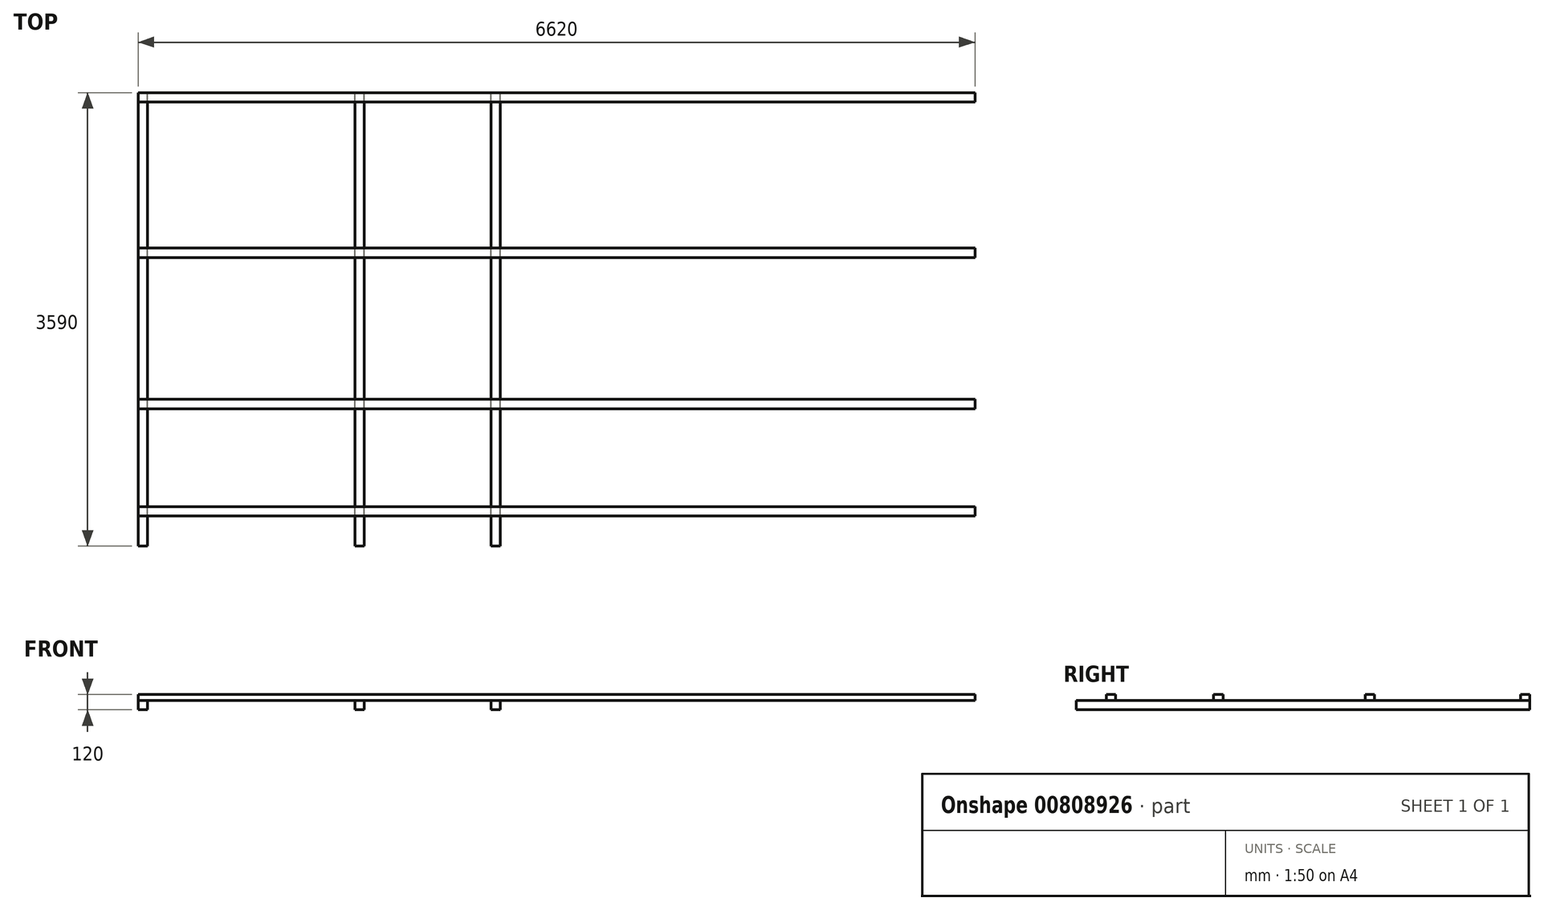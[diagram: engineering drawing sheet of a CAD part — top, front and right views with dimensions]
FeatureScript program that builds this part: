
annotation { "Feature Type Name" : "Feature", "Feature Type Description" : "" }
export const myFeature = defineFeature(function(context is Context, id is Id, definition is map)
    precondition{}
    {
        {
            var Q0;
            Q0=qCreatedBy(makeId("Front.planeOp"),FACE);
            var sketch = newSketch(context, id + "F0", { "sketchPlane" : qUnion([Q0])});
            skLineSegment(sketch, "E0.bottom", {"start": v(0, -75) * mm, "end": v(75, -75) * mm});
            skLineSegment(sketch, "E0.top", {"start": v(0, 0) * mm, "end": v(75, 0) * mm});
            skLineSegment(sketch, "E0.left", {"start": v(0, -75) * mm, "end": v(0, 0) * mm});
            skLineSegment(sketch, "E0.right", {"start": v(75, -75) * mm, "end": v(75, 0) * mm});
            skLineSegment(sketch, "E1.bottom", {"start": v(1714.03, -75) * mm, "end": v(1789.03, -75) * mm});
            skLineSegment(sketch, "E1.top", {"start": v(1714.03, 0) * mm, "end": v(1789.03, 0) * mm});
            skLineSegment(sketch, "E1.left", {"start": v(1714.03, -75) * mm, "end": v(1714.03, 0) * mm});
            skLineSegment(sketch, "E1.right", {"start": v(1789.03, -75) * mm, "end": v(1789.03, 0) * mm});
            skLineSegment(sketch, "E2.bottom", {"start": v(2790.5, -75) * mm, "end": v(2865.5, -75) * mm});
            skLineSegment(sketch, "E2.top", {"start": v(2790.5, 0) * mm, "end": v(2865.5, 0) * mm});
            skLineSegment(sketch, "E2.left", {"start": v(2790.5, -75) * mm, "end": v(2790.5, 0) * mm});
            skLineSegment(sketch, "E2.right", {"start": v(2865.5, -75) * mm, "end": v(2865.5, 0) * mm});
            skSolve(sketch);
        }
        {
            var Q0;
            Q0=qCreatedBy(makeId("Top.planeOp"),FACE);
            var sketch = newSketch(context, id + "F1", { "sketchPlane" : qUnion([Q0])});
            skLineSegment(sketch, "E3.top", {"start": v(0, 0) * mm, "end": v(6620, 0) * mm});
            skLineSegment(sketch, "E4.MirrorCS", {"start": v(6620, -75) * mm, "end": v(6620, 0) * mm});
            skLineSegment(sketch, "E5.MirrorCS", {"start": v(6620, -2502.27) * mm, "end": v(6620, -2427.27) * mm});
            skLineSegment(sketch, "E6.MirrorCS", {"start": v(0, -2502.27) * mm, "end": v(0, -2427.27) * mm});
            skLineSegment(sketch, "E7.MirrorCS", {"start": v(0, -1304.62) * mm, "end": v(0, -1229.62) * mm});
            skLineSegment(sketch, "E8.MirrorCS", {"start": v(6620, -1304.62) * mm, "end": v(6620, -1229.62) * mm});
            skLineSegment(sketch, "E9.MirrorCS", {"start": v(0, -1229.62) * mm, "end": v(6620, -1229.62) * mm});
            skLineSegment(sketch, "E10.MirrorCS", {"start": v(0, -1304.62) * mm, "end": v(6620, -1304.62) * mm});
            skLineSegment(sketch, "E11.MirrorCS", {"start": v(0, -2427.27) * mm, "end": v(6620, -2427.27) * mm});
            skLineSegment(sketch, "E12.MirrorCS", {"start": v(0, -2502.27) * mm, "end": v(6620, -2502.27) * mm});
            skLineSegment(sketch, "E13.MirrorCS", {"start": v(0, -75) * mm, "end": v(6620, -75) * mm});
            skLineSegment(sketch, "E14.MirrorCS", {"start": v(0, -75) * mm, "end": v(0, 0) * mm});
            skLineSegment(sketch, "E15.MirrorCS", {"start": v(6620, -3352.27) * mm, "end": v(6620, -3277.27) * mm});
            skLineSegment(sketch, "E16.MirrorCS", {"start": v(0, -3352.27) * mm, "end": v(0, -3277.27) * mm});
            skLineSegment(sketch, "E17.MirrorCS", {"start": v(0, -3277.27) * mm, "end": v(6620, -3277.27) * mm});
            skLineSegment(sketch, "E18.MirrorCS", {"start": v(0, -3352.27) * mm, "end": v(6620, -3352.27) * mm});
            skSolve(sketch);
        }
        {
            var Q0;
            Q0=makeQuery(id+"F0.imprint","IMPRINT",FACE,{"disambiguationData":[TD([[makeQuery(id+"F0.imprint","IMPRINT",EDGE,{"derivedFrom":sQuery(id+"F0.wireOp",EDGE,"E0.bottom")}),1.0]])]});
            var Q1;
            Q1=makeQuery(id+"F0.imprint","IMPRINT",FACE,{"disambiguationData":[TD([[makeQuery(id+"F0.imprint","IMPRINT",EDGE,{"derivedFrom":sQuery(id+"F0.wireOp",EDGE,"E2.bottom")}),1.0]])]});
            var Q2;
            Q2=makeQuery(id+"F0.imprint","IMPRINT",FACE,{"disambiguationData":[TD([[makeQuery(id+"F0.imprint","IMPRINT",EDGE,{"derivedFrom":sQuery(id+"F0.wireOp",EDGE,"E1.bottom")}),1.0]])]});
            extrude(context, id + "F2", {"entities" : qUnion([Q0, Q1, Q2]), "depth" : 3590 * mm, "offsetDistance" : 25 * mm});
        }
        {
            var Q0;
            Q0 = qSketchRegion(id + "F1", true);
            extrude(context, id + "F3", {"entities" : qUnion([Q0]), "depth" : 45 * mm, "offsetDistance" : 25 * mm});
        }
    });
